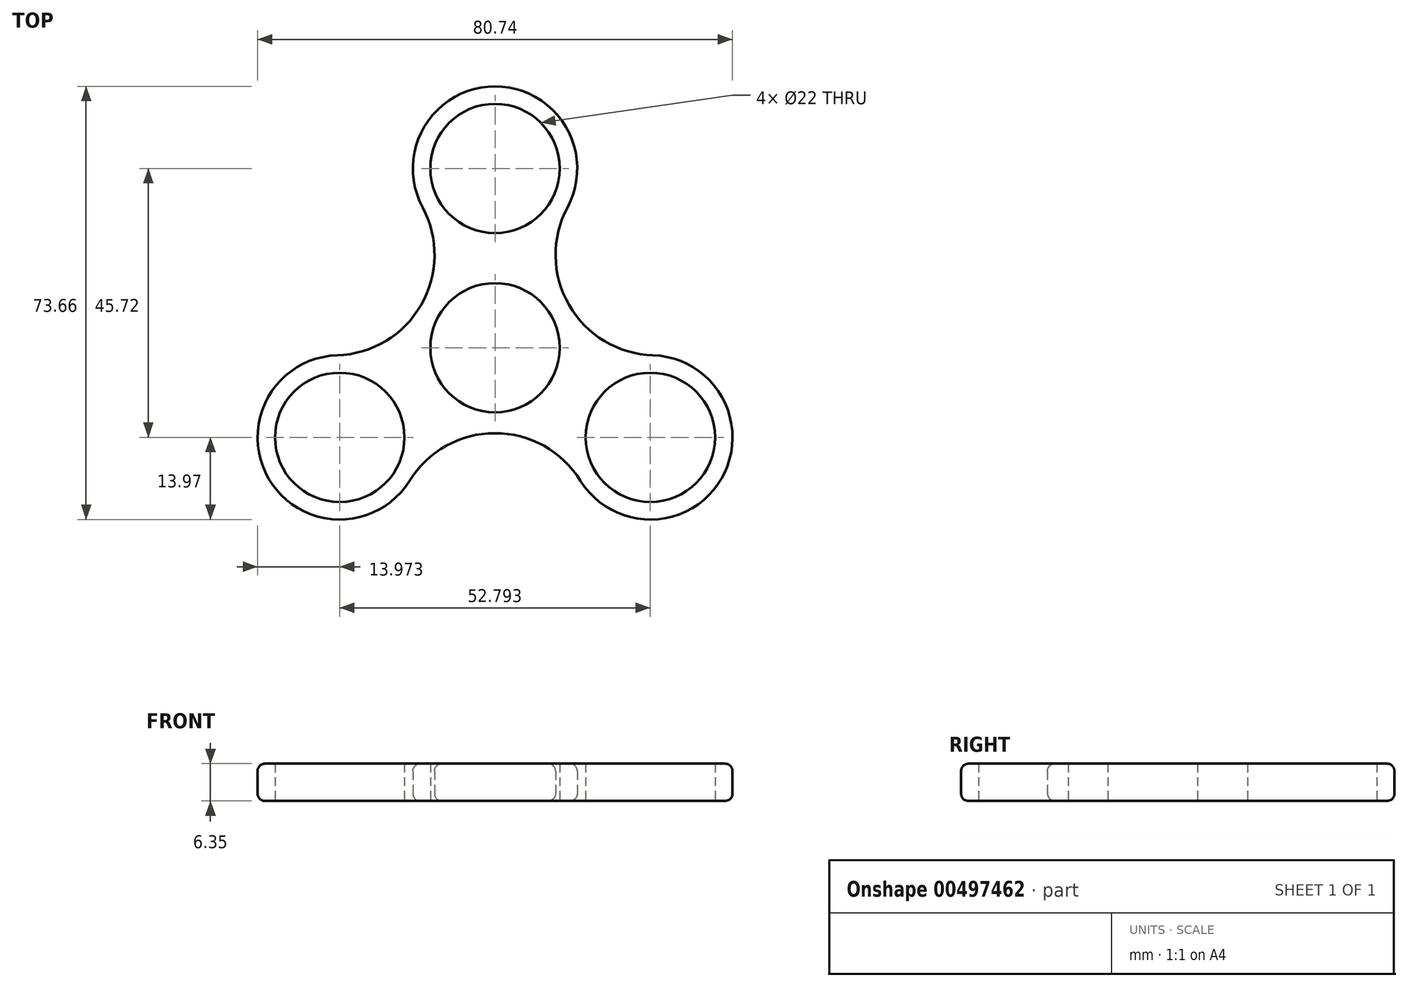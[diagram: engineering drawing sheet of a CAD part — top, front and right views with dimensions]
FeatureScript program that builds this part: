
annotation { "Feature Type Name" : "Feature", "Feature Type Description" : "" }
export const myFeature = defineFeature(function(context is Context, id is Id, definition is map)
    precondition{}
    {
        {
            var Q0;
            Q0=qCreatedBy(makeId("Top.planeOp"),FACE);
            var sketch = newSketch(context, id + "F0", { "sketchPlane" : qUnion([Q0])});
            skCircle(sketch, "E0", {"center": v(0, 0) * mm, "radius": 44.45 * mm});
            skCircle(sketch, "E1", {"center": v(0, 0) * mm, "radius": 11 * mm});
            skCircle(sketch, "E2", {"center": v(0, 30.48) * mm, "radius": 11 * mm});
            skCircle(sketch, "E3.1.0", {"center": v(-26.4, -15.24) * mm, "radius": 11 * mm});
            skCircle(sketch, "E3.2.0", {"center": v(26.4, -15.24) * mm, "radius": 11 * mm});
            skCircle(sketch, "E4", {"center": v(0, 30.48) * mm, "radius": 13.97 * mm});
            skCircle(sketch, "E5", {"center": v(-26.4, -15.24) * mm, "radius": 13.97 * mm});
            skCircle(sketch, "E6", {"center": v(26.4, -15.24) * mm, "radius": 13.97 * mm});
            skCircle(sketch, "E7", {"center": v(0, 0) * mm, "radius": 13.97 * mm});
            skArc(sketch, "E8", {"start": v(-26.84, -1.28) * mm, "mid": v(-12.58, 7.26) * mm, "end": v(-12.31, 23.88) * mm});
            skArc(sketch, "E9", {"start": v(12.31, 23.88) * mm, "mid": v(12.58, 7.26) * mm, "end": v(26.84, -1.28) * mm});
            skArc(sketch, "E10", {"start": v(14.53, -22.6) * mm, "mid": v(0, -14.52) * mm, "end": v(-14.53, -22.6) * mm});
            skSolve(sketch);
        }
        {
            var Q0;
            Q0=makeQuery(id+"F0.imprint","IMPRINT",FACE,{"disambiguationData":[TD([[makeQuery(id+"F0.imprint","IMPRINT",EDGE,{"derivedFrom":sQuery(id+"F0.wireOp",EDGE,"E2")}),-1.0]])]});
            var Q1;
            Q1=makeQuery(id+"F0.imprint","IMPRINT",FACE,{"disambiguationData":[TD([[makeQuery(id+"F0.imprint","IMPRINT",EDGE,{"derivedFrom":sQuery(id+"F0.wireOp",EDGE,"E3.2.0")}),-1.0]])]});
            var Q2;
            Q2=makeQuery(id+"F0.imprint","IMPRINT",FACE,{"disambiguationData":[TD([[makeQuery(id+"F0.imprint","IMPRINT",EDGE,{"derivedFrom":sQuery(id+"F0.wireOp",EDGE,"E3.1.0")}),-1.0]])]});
            var Q3;
            Q3=makeQuery(id+"F0.imprint","IMPRINT",FACE,{"disambiguationData":[TD([[makeQuery(id+"F0.imprint","IMPRINT",EDGE,{"derivedFrom":sQuery(id+"F0.wireOp",EDGE,"E7")}),-1.0]])]});
            var Q4;
            Q4=makeQuery(id+"F0.imprint","IMPRINT",FACE,{"disambiguationData":[TD([[makeQuery(id+"F0.imprint","IMPRINT",EDGE,{"derivedFrom":sQuery(id+"F0.wireOp",EDGE,"E1")}),-1.0]])]});
            extrude(context, id + "F1", {"entities" : qUnion([Q0, Q1, Q2, Q3, Q4]), "depth" : 6.35 * mm});
        }
        {
            var Q0;
            Q0=makeQuery(id+"F1.opExtrude","CAP_EDGE",EDGE,{"disambiguationData":[OSD([sQuery(id+"F0.wireOp",EDGE,"E6")])],"isStart":false});
            var Q1;
            Q1=makeQuery(id+"F1.opExtrude","CAP_EDGE",EDGE,{"disambiguationData":[OSD([sQuery(id+"F0.wireOp",EDGE,"E6")])],"isStart":true});
            fillet(context, id + "F2", {"entities" : qUnion([Q0, Q1]), "radius" : 1.27 * mm, "tangentPropagation" : true, "allowEdgeOverflow" : false});
        }
    });
